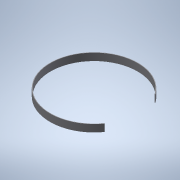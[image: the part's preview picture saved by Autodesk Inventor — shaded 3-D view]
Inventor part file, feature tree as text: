
AUTODESK INVENTOR PART (.ipt)
format: ipt  version: 2021 (Build 250183000, 183)  size: 225,280 bytes
history: native  units: mm
features: extrude x1, sketch x1
ambient origin geometry x8: Origin, YZ Plane, XZ Plane, XY Plane, X Axis, Y Axis, Z Axis, Center Point
bodies: Body1 (feature_tree)
feature tree (2):
  extrude  "Extrusion3"  Depth=50.0mm
  sketch  "Sketch1"  dims[d3=7.5mm d6=30.0mm d7=3.5mm d8=3.5mm d26=8.25mm d27=33.5mm d28=7.5mm d43=4.0mm d44=50.0mm d45=0.0mm d46=0.125mm d47=0.125mm]
